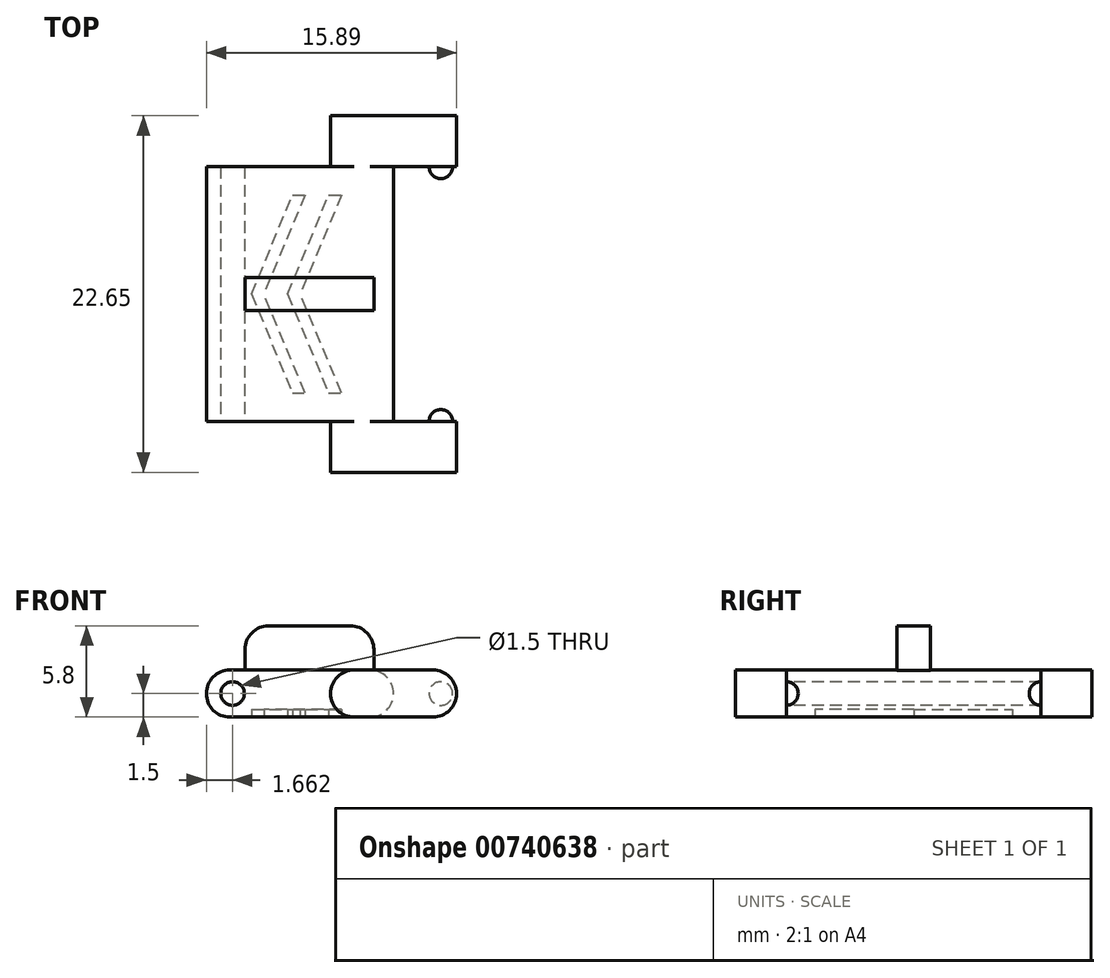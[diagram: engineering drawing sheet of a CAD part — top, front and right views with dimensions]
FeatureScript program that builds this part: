
annotation { "Feature Type Name" : "Feature", "Feature Type Description" : "" }
export const myFeature = defineFeature(function(context is Context, id is Id, definition is map)
    precondition{}
    {
        {
            var Q0;
            Q0=qCreatedBy(makeId("Top.planeOp"),FACE);
            var sketch = newSketch(context, id + "F0", { "sketchPlane" : qUnion([Q0])});
            skLineSegment(sketch, "E0.bottom", {"start": v(0, 0) * mm, "end": v(11.9, 0) * mm});
            skLineSegment(sketch, "E0.top", {"start": v(0, 16.17) * mm, "end": v(11.9, 16.17) * mm});
            skLineSegment(sketch, "E0.left", {"start": v(0, 0) * mm, "end": v(0, 16.17) * mm});
            skLineSegment(sketch, "E0.right", {"start": v(11.9, 0) * mm, "end": v(11.9, 16.17) * mm});
            skLineSegment(sketch, "E1.bottom", {"start": v(7.9, 16.17) * mm, "end": v(15.9, 16.17) * mm});
            skLineSegment(sketch, "E1.top", {"start": v(7.9, 19.41) * mm, "end": v(15.9, 19.41) * mm});
            skLineSegment(sketch, "E1.left", {"start": v(7.9, 16.17) * mm, "end": v(7.9, 19.41) * mm});
            skLineSegment(sketch, "E1.right", {"start": v(15.9, 16.17) * mm, "end": v(15.9, 19.41) * mm});
            skLineSegment(sketch, "E2.bottom", {"start": v(7.9, 0) * mm, "end": v(15.9, 0) * mm});
            skLineSegment(sketch, "E2.top", {"start": v(7.9, -3.24) * mm, "end": v(15.9, -3.24) * mm});
            skLineSegment(sketch, "E2.left", {"start": v(7.9, 0) * mm, "end": v(7.9, -3.24) * mm});
            skLineSegment(sketch, "E2.right", {"start": v(15.9, 0) * mm, "end": v(15.9, -3.24) * mm});
            skSolve(sketch);
        }
        {
            var Q0;
            {var subQ2=sQuery(id+"F0.wireOp",EDGE,"E0.bottom");Q0=makeQuery(id+"F0.imprint","IMPRINT",FACE,{"disambiguationData":[TD([[makeQuery(id+"F0.imprint","IMPRINT",EDGE,{"derivedFrom":subQ2}),1.0]])]});}
            var Q1;
            Q1=makeQuery(id+"F0.imprint","IMPRINT",FACE,{"disambiguationData":[TD([[makeQuery(id+"F0.imprint","IMPRINT",EDGE,{"derivedFrom":sQuery(id+"F0.wireOp",EDGE,"E1.top")}),-1.0]])]});
            var Q2;
            Q2=makeQuery(id+"F0.imprint","IMPRINT",FACE,{"disambiguationData":[TD([[makeQuery(id+"F0.imprint","IMPRINT",EDGE,{"derivedFrom":sQuery(id+"F0.wireOp",EDGE,"E2.top")}),1.0]])]});
            extrude(context, id + "F1", {"entities" : qUnion([Q0, Q1, Q2]), "depth" : 3 * mm, "offsetDistance" : 25 * mm});
        }
        {
            var Q0;
            Q0=makeQuery(id+"F1.opExtrude","SWEPT_FACE",FACE,{"disambiguationData":[OSD([sQuery(id+"F0.wireOp",EDGE,"E1.bottom")])]});
            var sketch = newSketch(context, id + "F2", { "sketchPlane" : qUnion([Q0])});
            skCircle(sketch, "E3", {"center": v(14.9, 1.5) * mm, "radius": 0.75 * mm});
            skPoint(sketch, "E3.centerSnap1", {"position": v(15.9, 1.5) * mm});
            skSolve(sketch);
        }
        {
            var Q0;
            Q0=makeQuery(id+"F2.imprint","IMPRINT",FACE,{"disambiguationData":[TD([[makeQuery(id+"F2.imprint","IMPRINT",EDGE,{"derivedFrom":sQuery(id+"F2.wireOp",EDGE,"E3")}),1.0]])]});
            extrude(context, id + "F3", {"entities" : qUnion([Q0]), "operationType" : NewBodyOperationType.ADD, "depth" : 0.75 * mm, "offsetDistance" : 25 * mm});
        }
        {
            var Q0;
            Q0=makeQuery(id+"F1.opExtrude","SWEPT_FACE",FACE,{"disambiguationData":[OSD([sQuery(id+"F0.wireOp",EDGE,"E2.bottom")])]});
            var sketch = newSketch(context, id + "F4", { "sketchPlane" : qUnion([Q0])});
            skCircle(sketch, "E4", {"center": v(-14.9, 1.5) * mm, "radius": 0.75 * mm});
            skPoint(sketch, "E4.centerSnap0", {"position": v(-15.9, 1.5) * mm});
            skSolve(sketch);
        }
        {
            var Q0;
            Q0=makeQuery(id+"F4.imprint","IMPRINT",FACE,{"disambiguationData":[TD([[makeQuery(id+"F4.imprint","IMPRINT",EDGE,{"derivedFrom":sQuery(id+"F4.wireOp",EDGE,"E4")}),1.0]])]});
            extrude(context, id + "F5", {"entities" : qUnion([Q0]), "operationType" : NewBodyOperationType.ADD, "depth" : 0.75 * mm, "offsetDistance" : 25 * mm});
        }
        {
            var Q0;
            Q0=makeQuery(id+"F1.opExtrude","SWEPT_FACE",FACE,{"disambiguationData":[OSD([sQuery(id+"F0.wireOp",EDGE,"E0.bottom")])]});
            var sketch = newSketch(context, id + "F6", { "sketchPlane" : qUnion([Q0])});
            skCircle(sketch, "E5", {"center": v(1.66, 1.5) * mm, "radius": 0.75 * mm});
            skPoint(sketch, "E5.centerSnap0", {"position": v(0, 1.5) * mm});
            skSolve(sketch);
        }
        {
            var Q0;
            Q0=makeQuery(id+"F6.imprint","IMPRINT",FACE,{"disambiguationData":[TD([[makeQuery(id+"F6.imprint","IMPRINT",EDGE,{"derivedFrom":sQuery(id+"F6.wireOp",EDGE,"E5")}),1.0]])]});
            extrude(context, id + "F7", {"entities" : qUnion([Q0]), "operationType" : NewBodyOperationType.REMOVE, "oppositeDirection" : true, "depth" : 25 * mm, "offsetDistance" : 25 * mm});
        }
        {
            var Q0;
            Q0=makeQuery(id+"F1.opExtrude","CAP_EDGE",EDGE,{"disambiguationData":[OSD([sQuery(id+"F0.wireOp",EDGE,"E0.left")])],"isStart":false});
            var Q1;
            Q1=makeQuery(id+"F1.opExtrude","CAP_EDGE",EDGE,{"disambiguationData":[OSD([sQuery(id+"F0.wireOp",EDGE,"E0.left")])],"isStart":true});
            var Q2;
            Q2=makeQuery(id+"F1.opExtrude","CAP_EDGE",EDGE,{"disambiguationData":[OSD([sQuery(id+"F0.wireOp",EDGE,"E1.right")])],"isStart":false});
            var Q3;
            Q3=makeQuery(id+"F1.opExtrude","CAP_EDGE",EDGE,{"disambiguationData":[OSD([sQuery(id+"F0.wireOp",EDGE,"E1.right")])],"isStart":true});
            var Q4;
            Q4=makeQuery(id+"F1.opExtrude","CAP_EDGE",EDGE,{"disambiguationData":[OSD([sQuery(id+"F0.wireOp",EDGE,"E2.right")])],"isStart":false});
            var Q5;
            Q5=makeQuery(id+"F1.opExtrude","CAP_EDGE",EDGE,{"disambiguationData":[OSD([sQuery(id+"F0.wireOp",EDGE,"E2.right")])],"isStart":true});
            fillet(context, id + "F8", {"entities" : qUnion([Q0, Q1, Q2, Q3, Q4, Q5]), "radius" : 1.5 * mm, "tangentPropagation" : true, "allowEdgeOverflow" : false});
        }
        {
            var Q0;
            Q0=makeQuery(id+"F1.opExtrude","CAP_FACE",FACE,{"disambiguationData":[OSD([sQuery(id+"F0.wireOp",EDGE,"E0.bottom"),sQuery(id+"F0.wireOp",EDGE,"E0.top"),sQuery(id+"F0.wireOp",EDGE,"E0.left"),sQuery(id+"F0.wireOp",EDGE,"E0.right"),sQuery(id+"F0.wireOp",EDGE,"E1.bottom"),sQuery(id+"F0.wireOp",EDGE,"E1.top"),sQuery(id+"F0.wireOp",EDGE,"E1.left"),sQuery(id+"F0.wireOp",EDGE,"E1.right"),sQuery(id+"F0.wireOp",EDGE,"E2.bottom"),sQuery(id+"F0.wireOp",EDGE,"E2.top"),sQuery(id+"F0.wireOp",EDGE,"E2.left"),sQuery(id+"F0.wireOp",EDGE,"E2.right")])],"isStart":false});
            var sketch = newSketch(context, id + "F9", { "sketchPlane" : qUnion([Q0])});
            skLineSegment(sketch, "E6.bottom", {"start": v(2.45, 9.14) * mm, "end": v(10.63, 9.14) * mm});
            skLineSegment(sketch, "E6.top", {"start": v(2.45, 7.03) * mm, "end": v(10.63, 7.03) * mm});
            skLineSegment(sketch, "E6.left", {"start": v(2.45, 9.14) * mm, "end": v(2.45, 7.03) * mm});
            skLineSegment(sketch, "E6.right", {"start": v(10.63, 9.14) * mm, "end": v(10.63, 7.03) * mm});
            skPoint(sketch, "E6.middle", {"position": v(6.54, 8.08) * mm});
            skPoint(sketch, "E6.middle.positionSnap0", {"position": v(1.5, 8.08) * mm});
            skPoint(sketch, "E6.centerSnap0", {"position": v(1.5, 8.08) * mm});
            skSolve(sketch);
        }
        {
            var Q0;
            Q0=makeQuery(id+"F9.imprint","IMPRINT",FACE,{"disambiguationData":[TD([[makeQuery(id+"F9.imprint","IMPRINT",EDGE,{"derivedFrom":sQuery(id+"F9.wireOp",EDGE,"E6.bottom")}),-1.0]])]});
            extrude(context, id + "F10", {"entities" : qUnion([Q0]), "operationType" : NewBodyOperationType.ADD, "depth" : 2.8 * mm, "offsetDistance" : 25 * mm});
        }
        {
            var Q0;
            Q0=makeQuery(id+"F10.opExtrude","CAP_EDGE",EDGE,{"disambiguationData":[OSD([sQuery(id+"F9.wireOp",EDGE,"E6.right")])],"isStart":false});
            var Q1;
            Q1=makeQuery(id+"F10.opExtrude","CAP_EDGE",EDGE,{"disambiguationData":[OSD([sQuery(id+"F9.wireOp",EDGE,"E6.left")])],"isStart":false});
            fillet(context, id + "F11", {"entities" : qUnion([Q0, Q1]), "radius" : 1.5 * mm, "tangentPropagation" : true, "allowEdgeOverflow" : false});
        }
        {
            var Q0;
            Q0=makeQuery(id+"F1.opExtrude","CAP_FACE",FACE,{"disambiguationData":[OSD([sQuery(id+"F0.wireOp",EDGE,"E0.bottom"),sQuery(id+"F0.wireOp",EDGE,"E0.top"),sQuery(id+"F0.wireOp",EDGE,"E0.left"),sQuery(id+"F0.wireOp",EDGE,"E0.right"),sQuery(id+"F0.wireOp",EDGE,"E1.bottom"),sQuery(id+"F0.wireOp",EDGE,"E1.top"),sQuery(id+"F0.wireOp",EDGE,"E1.left"),sQuery(id+"F0.wireOp",EDGE,"E1.right"),sQuery(id+"F0.wireOp",EDGE,"E2.bottom"),sQuery(id+"F0.wireOp",EDGE,"E2.top"),sQuery(id+"F0.wireOp",EDGE,"E2.left"),sQuery(id+"F0.wireOp",EDGE,"E2.right")])],"isStart":true});
            var sketch = newSketch(context, id + "F12", { "sketchPlane" : qUnion([Q0])});
            skLineSegment(sketch, "E7", {"start": v(2.87, -8.08) * mm, "end": v(5.46, -14.37) * mm});
            skPoint(sketch, "E7.startSnap0", {"position": v(1.5, -8.08) * mm});
            skLineSegment(sketch, "E8", {"start": v(5.46, -14.37) * mm, "end": v(6.28, -14.37) * mm});
            skLineSegment(sketch, "E9", {"start": v(6.28, -14.37) * mm, "end": v(3.65, -8.08) * mm});
            skLineSegment(sketch, "E10.MirrorCS", {"start": v(2.87, -8.08) * mm, "end": v(5.46, -1.8) * mm});
            skLineSegment(sketch, "E11.MirrorCS", {"start": v(6.28, -1.8) * mm, "end": v(3.65, -8.08) * mm});
            skLineSegment(sketch, "E12.MirrorCS", {"start": v(5.46, -1.8) * mm, "end": v(6.28, -1.8) * mm});
            skLineSegment(sketch, "E13.1.0.0", {"start": v(5.17, -8.08) * mm, "end": v(7.76, -14.37) * mm});
            skLineSegment(sketch, "E13.1.0.1", {"start": v(8.58, -14.37) * mm, "end": v(5.95, -8.08) * mm});
            skLineSegment(sketch, "E13.1.0.2", {"start": v(7.76, -14.37) * mm, "end": v(8.58, -14.37) * mm});
            skLineSegment(sketch, "E13.1.0.3", {"start": v(5.17, -8.08) * mm, "end": v(7.76, -1.8) * mm});
            skLineSegment(sketch, "E13.1.0.4", {"start": v(8.58, -1.8) * mm, "end": v(5.95, -8.08) * mm});
            skLineSegment(sketch, "E13.1.0.5", {"start": v(7.76, -1.8) * mm, "end": v(8.58, -1.8) * mm});
            skLineSegment(sketch, "E13.direction1", {"start": v(5.46, -14.37) * mm, "end": v(7.76, -14.37) * mm, "construction": true});
            skSolve(sketch);
        }
        {
            var Q0;
            Q0=makeQuery(id+"F12.imprint","IMPRINT",FACE,{"disambiguationData":[TD([[makeQuery(id+"F12.imprint","IMPRINT",EDGE,{"derivedFrom":sQuery(id+"F12.wireOp",EDGE,"E7")}),1.0]])]});
            var Q1;
            Q1=makeQuery(id+"F12.imprint","IMPRINT",FACE,{"disambiguationData":[TD([[makeQuery(id+"F12.imprint","IMPRINT",EDGE,{"derivedFrom":sQuery(id+"F12.wireOp",EDGE,"E13.1.0.0")}),1.0]])]});
            var Q2;
            Q2=makeQuery(id+"F12.imprint","IMPRINT",FACE,{"disambiguationData":[TD([[makeQuery(id+"F12.imprint","IMPRINT",EDGE,{"derivedFrom":sQuery(id+"F12.wireOp",EDGE,"E13.2.0.0")}),1.0]])]});
            extrude(context, id + "F13", {"entities" : qUnion([Q0, Q1, Q2]), "operationType" : NewBodyOperationType.REMOVE, "oppositeDirection" : true, "depth" : 0.5 * mm, "offsetDistance" : 25 * mm});
        }
        {
            var Q0;
            Q0=makeQuery(id+"F5.opExtrude","CAP_EDGE",EDGE,{"disambiguationData":[OSD([sQuery(id+"F4.wireOp",EDGE,"E4")])],"isStart":false});
            var Q1;
            Q1=makeQuery(id+"F3.opExtrude","CAP_EDGE",EDGE,{"disambiguationData":[OSD([sQuery(id+"F2.wireOp",EDGE,"E3")])],"isStart":false});
            fillet(context, id + "F14", {"entities" : qUnion([Q0, Q1]), "radius" : 0.75 * mm, "tangentPropagation" : true, "allowEdgeOverflow" : false});
        }
        {
            var Q0;
            Q0=makeQuery(id+"F1.opExtrude","CAP_EDGE",EDGE,{"disambiguationData":[OSD([sQuery(id+"F0.wireOp",EDGE,"E0.right")])],"isStart":false});
            var Q1;
            Q1=makeQuery(id+"F1.opExtrude","CAP_EDGE",EDGE,{"disambiguationData":[OSD([sQuery(id+"F0.wireOp",EDGE,"E0.right")])],"isStart":true});
            fillet(context, id + "F15", {"entities" : qUnion([Q0, Q1]), "radius" : 1.5 * mm, "tangentPropagation" : true, "allowEdgeOverflow" : false});
        }
        {
            var Q0;
            Q0=makeQuery(id+"F1.opExtrude","CAP_EDGE",EDGE,{"disambiguationData":[OSD([sQuery(id+"F0.wireOp",EDGE,"E2.left")])],"isStart":false});
            var Q1;
            Q1=makeQuery(id+"F1.opExtrude","CAP_EDGE",EDGE,{"disambiguationData":[OSD([sQuery(id+"F0.wireOp",EDGE,"E2.left")])],"isStart":true});
            var Q2;
            Q2=makeQuery(id+"F1.opExtrude","CAP_EDGE",EDGE,{"disambiguationData":[OSD([sQuery(id+"F0.wireOp",EDGE,"E1.left")])],"isStart":false});
            var Q3;
            Q3=makeQuery(id+"F1.opExtrude","CAP_EDGE",EDGE,{"disambiguationData":[OSD([sQuery(id+"F0.wireOp",EDGE,"E1.left")])],"isStart":true});
            fillet(context, id + "F16", {"entities" : qUnion([Q0, Q1, Q2, Q3]), "radius" : 1.5 * mm, "tangentPropagation" : true, "allowEdgeOverflow" : false});
        }
    });
